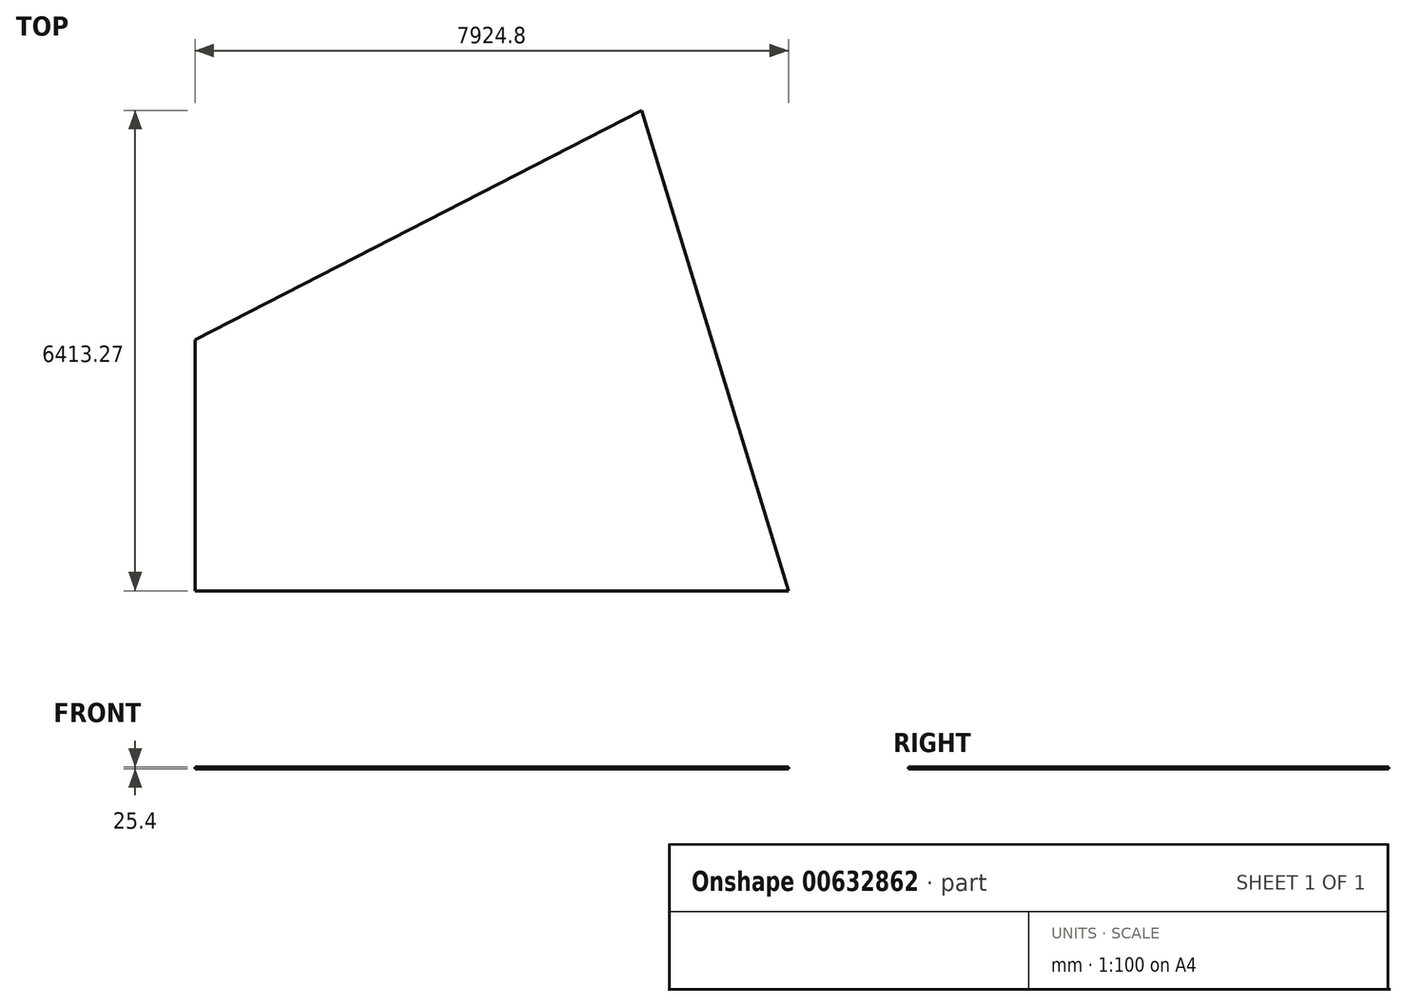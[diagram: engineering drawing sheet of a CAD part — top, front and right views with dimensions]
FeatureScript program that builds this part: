
annotation { "Feature Type Name" : "Feature", "Feature Type Description" : "" }
export const myFeature = defineFeature(function(context is Context, id is Id, definition is map)
    precondition{}
    {
        {
            var Q0;
            Q0=qCreatedBy(makeId("Top.planeOp"),FACE);
            var sketch = newSketch(context, id + "F0", { "sketchPlane" : qUnion([Q0])});
            skLineSegment(sketch, "E0", {"start": v(0, 0) * mm, "end": v(7924.8, 0) * mm});
            skLineSegment(sketch, "E1", {"start": v(7924.8, 0) * mm, "end": v(5966.46, 6413.27) * mm});
            skLineSegment(sketch, "E2", {"start": v(0, 3352.8) * mm, "end": v(0, 0) * mm});
            skLineSegment(sketch, "E3", {"start": v(5966.46, 6413.27) * mm, "end": v(0, 3352.8) * mm});
            skSolve(sketch);
        }
        {
            var Q0;
            Q0=makeQuery(id+"F0.imprint","IMPRINT",FACE,{"disambiguationData":[TD([[makeQuery(id+"F0.imprint","IMPRINT",EDGE,{"derivedFrom":sQuery(id+"F0.wireOp",EDGE,"E0")}),1.0]])]});
            extrude(context, id + "F1", {"entities" : qUnion([Q0]), "depth" : 25.4 * mm, "offsetDistance" : 25.4 * mm});
        }
    });
